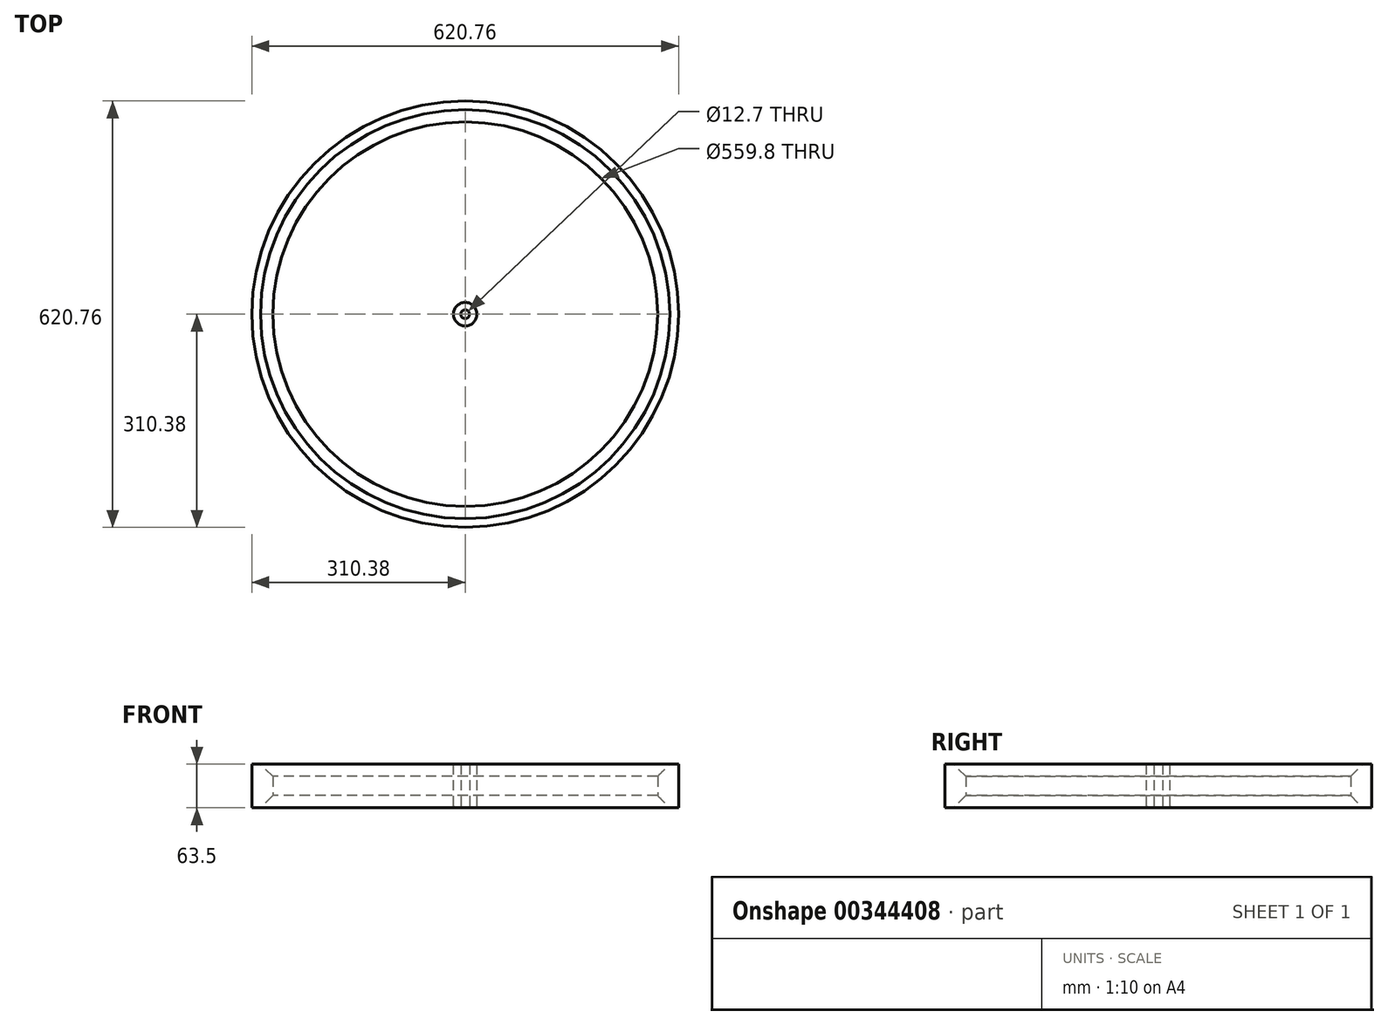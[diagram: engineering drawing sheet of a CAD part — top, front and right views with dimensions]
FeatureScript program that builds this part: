
annotation { "Feature Type Name" : "Feature", "Feature Type Description" : "" }
export const myFeature = defineFeature(function(context is Context, id is Id, definition is map)
    precondition{}
    {
        {
            var Q0;
            Q0=qCreatedBy(makeId("Top.planeOp"),FACE);
            var sketch = newSketch(context, id + "F0", { "sketchPlane" : qUnion([Q0])});
            skCircle(sketch, "E0", {"center": v(0, 0) * mm, "radius": 310.38 * mm});
            skSolve(sketch);
        }
        {
            var Q0;
            Q0=makeQuery(id+"F0.imprint","IMPRINT",FACE,{"disambiguationData":[TD([[makeQuery(id+"F0.imprint","IMPRINT",EDGE,{"derivedFrom":sQuery(id+"F0.wireOp",EDGE,"E0")}),1.0]])]});
            extrude(context, id + "F1", {"entities" : qUnion([Q0]), "endBound" : BoundingType.SYMMETRIC, "depth" : 63.5 * mm});
        }
        {
            var Q0;
            Q0=makeQuery(id+"F1.opExtrude","CAP_FACE",FACE,{"disambiguationData":[OSD([sQuery(id+"F0.wireOp",EDGE,"E0")])],"isStart":false});
            var sketch = newSketch(context, id + "F2", { "sketchPlane" : qUnion([Q0])});
            skCircle(sketch, "E1", {"center": v(0, 0) * mm, "radius": 267.57 * mm});
            skCircle(sketch, "E2", {"center": v(0, 0) * mm, "radius": 17.1 * mm});
            skSolve(sketch);
        }
        {
            var Q0;
            Q0=makeQuery(id+"F1.opExtrude","CAP_FACE",FACE,{"disambiguationData":[OSD([sQuery(id+"F0.wireOp",EDGE,"E0")])],"isStart":false});
            var Q1;
            Q1=makeQuery(id+"F1.opExtrude","CAP_FACE",FACE,{"disambiguationData":[OSD([sQuery(id+"F0.wireOp",EDGE,"E0")])],"isStart":true});
            var Q2;
            Q2=makeQuery(id+"F1.opExtrude","SWEPT_BODY",BODY,{"disambiguationData":[OSD([sQuery(id+"F0.wireOp",EDGE,"E0")])]});
            shell(context, id + "F3", {"entities" : qUnion([Q0, Q1]), "parts" : qUnion([Q2]), "thickness" : 30.48 * mm});
        }
        {
            var Q0;
            Q0=makeQuery(id+"F2.imprint","IMPRINT",FACE,{"disambiguationData":[TD([[makeQuery(id+"F2.imprint","IMPRINT",EDGE,{"derivedFrom":sQuery(id+"F2.wireOp",EDGE,"E2")}),1.0]])]});
            extrude(context, id + "F4", {"entities" : qUnion([Q0]), "oppositeDirection" : true, "depth" : 63.5 * mm});
        }
        {
            var Q0;
            Q0=makeQuery(id+"F4.opExtrude","SWEPT_FACE",FACE,{"disambiguationData":[OSD([sQuery(id+"F2.wireOp",EDGE,"E2")])]});
            fillet(context, id + "F5", {"entities" : qUnion([Q0]), "radius" : 2.54 * mm, "tangentPropagation" : true, "allowEdgeOverflow" : false});
        }
        {
            var Q0;
            Q0=qCreatedBy(makeId("Top.planeOp"),FACE);
            var sketch = newSketch(context, id + "F6", { "sketchPlane" : qUnion([Q0])});
            skLineSegment(sketch, "E3", {"start": v(203.69, 189.84) * mm, "end": v(0, 0) * mm});
            skLineSegment(sketch, "E4", {"start": v(0, 0) * mm, "end": v(0, 279.46) * mm});
            skLineSegment(sketch, "E5", {"start": v(0, 279.46) * mm, "end": v(0, -279.46) * mm});
            skLineSegment(sketch, "E6", {"start": v(0, 0) * mm, "end": v(279.46, 0) * mm});
            skLineSegment(sketch, "E7", {"start": v(279.46, 0) * mm, "end": v(-279.46, 0) * mm});
            skLineSegment(sketch, "E8.MirrorCS", {"start": v(203.69, -189.84) * mm, "end": v(0, 0) * mm});
            skLineSegment(sketch, "E9.MirrorCS", {"start": v(-203.69, 189.84) * mm, "end": v(0, 0) * mm});
            skLineSegment(sketch, "E10.MirrorCS", {"start": v(-203.69, -189.84) * mm, "end": v(0, 0) * mm});
            skLineSegment(sketch, "E11.MirrorCS", {"start": v(-279.46, 0) * mm, "end": v(279.46, 0) * mm});
            skLineSegment(sketch, "E12.MirrorCS", {"start": v(0, -279.46) * mm, "end": v(0, 279.46) * mm});
            skLineSegment(sketch, "E13", {"start": v(263.16, 96.14) * mm, "end": v(0, 0) * mm});
            skLineSegment(sketch, "E14.MirrorCS", {"start": v(263.16, -96.14) * mm, "end": v(0, 0) * mm});
            skLineSegment(sketch, "E15.MirrorCS", {"start": v(-263.16, 96.14) * mm, "end": v(0, 0) * mm});
            skLineSegment(sketch, "E16.MirrorCS", {"start": v(-263.16, -96.14) * mm, "end": v(0, 0) * mm});
            skLineSegment(sketch, "E17", {"start": v(123.37, 250.75) * mm, "end": v(0, 0) * mm});
            skLineSegment(sketch, "E18.MirrorCS", {"start": v(123.37, -250.75) * mm, "end": v(0, 0) * mm});
            skLineSegment(sketch, "E19.MirrorCS", {"start": v(-123.37, 250.75) * mm, "end": v(0, 0) * mm});
            skLineSegment(sketch, "E20.MirrorCS", {"start": v(-123.37, -250.75) * mm, "end": v(0, 0) * mm});
            skArc(sketch, "E21", {"start": v(123.37, 250.75) * mm, "mid": v(63.34, 272.19) * mm, "end": v(0, 279.46) * mm});
            skArc(sketch, "E22", {"start": v(-123.37, 250.75) * mm, "mid": v(-63.34, 272.19) * mm, "end": v(0, 279.46) * mm});
            skArc(sketch, "E23", {"start": v(-203.69, 189.84) * mm, "mid": v(-166.04, 223.51) * mm, "end": v(-122.92, 249.83) * mm});
            skArc(sketch, "E24", {"start": v(-203.69, 189.84) * mm, "mid": v(-237.34, 145.6) * mm, "end": v(-261.53, 95.54) * mm});
            skArc(sketch, "E25", {"start": v(-279.46, 0) * mm, "mid": v(-275.18, 48.7) * mm, "end": v(-262.49, 95.9) * mm});
            skArc(sketch, "E26", {"start": v(203.69, 189.84) * mm, "mid": v(166.04, 223.51) * mm, "end": v(122.92, 249.83) * mm});
            skArc(sketch, "E27.MirrorCS", {"start": v(203.69, 189.84) * mm, "mid": v(237.34, 145.6) * mm, "end": v(261.53, 95.54) * mm});
            skArc(sketch, "E28.MirrorCS", {"start": v(279.46, 0) * mm, "mid": v(275.18, 48.7) * mm, "end": v(262.49, 95.9) * mm});
            skArc(sketch, "E29.MirrorCS", {"start": v(-279.46, 0) * mm, "mid": v(-275.18, -48.7) * mm, "end": v(-262.49, -95.9) * mm});
            skArc(sketch, "E30.MirrorCS", {"start": v(-203.69, -189.84) * mm, "mid": v(-237.34, -145.6) * mm, "end": v(-261.53, -95.54) * mm});
            skArc(sketch, "E31.MirrorCS", {"start": v(-203.69, -189.84) * mm, "mid": v(-166.04, -223.51) * mm, "end": v(-122.92, -249.83) * mm});
            skArc(sketch, "E32.MirrorCS", {"start": v(-123.37, -250.75) * mm, "mid": v(-63.34, -272.19) * mm, "end": v(0, -279.46) * mm});
            skArc(sketch, "E33.MirrorCS", {"start": v(123.37, -250.75) * mm, "mid": v(63.34, -272.19) * mm, "end": v(0, -279.46) * mm});
            skArc(sketch, "E34.MirrorCS", {"start": v(203.69, -189.84) * mm, "mid": v(166.04, -223.51) * mm, "end": v(122.92, -249.83) * mm});
            skArc(sketch, "E35.MirrorCS", {"start": v(203.69, -189.84) * mm, "mid": v(237.34, -145.6) * mm, "end": v(261.53, -95.54) * mm});
            skArc(sketch, "E36.MirrorCS", {"start": v(279.46, 0) * mm, "mid": v(275.18, -48.7) * mm, "end": v(262.49, -95.9) * mm});
            skSolve(sketch);
        }
        {
            var Q0;
            {var subQ0=sQuery(id+"F6.wireOp",EDGE,"E3");Q0=makeQuery(id+"F6.imprint","IMPRINT",FACE,{"disambiguationData":[TD([[makeQuery(id+"F6.imprint","IMPRINT",EDGE,{"derivedFrom":subQ0}),1.0]])]});}
            var Q1;
            {var subQ0=sQuery(id+"F6.wireOp",EDGE,"E3");Q1=makeQuery(id+"F6.imprint","IMPRINT",FACE,{"disambiguationData":[TD([[makeQuery(id+"F6.imprint","IMPRINT",EDGE,{"derivedFrom":subQ0}),-1.0]])]});}
            var Q2;
            {var subQ0=sQuery(id+"F6.wireOp",EDGE,"E21");Q2=makeQuery(id+"F6.imprint","IMPRINT",FACE,{"disambiguationData":[TD([[makeQuery(id+"F6.imprint","IMPRINT",EDGE,{"derivedFrom":subQ0}),1.0]])]});}
            var Q3;
            {var subQ4=sQuery(id+"F6.wireOp",EDGE,"E22");Q3=makeQuery(id+"F6.imprint","IMPRINT",FACE,{"disambiguationData":[TD([[makeQuery(id+"F6.imprint","IMPRINT",EDGE,{"derivedFrom":subQ4}),-1.0]])]});}
            var Q4;
            {var subQ0=sQuery(id+"F6.wireOp",EDGE,"E9.MirrorCS");Q4=makeQuery(id+"F6.imprint","IMPRINT",FACE,{"disambiguationData":[TD([[makeQuery(id+"F6.imprint","IMPRINT",EDGE,{"derivedFrom":subQ0}),1.0]])]});}
            var Q5;
            {var subQ0=sQuery(id+"F6.wireOp",EDGE,"E9.MirrorCS");Q5=makeQuery(id+"F6.imprint","IMPRINT",FACE,{"disambiguationData":[TD([[makeQuery(id+"F6.imprint","IMPRINT",EDGE,{"derivedFrom":subQ0}),-1.0]])]});}
            var Q6;
            {var subQ0=sQuery(id+"F6.wireOp",EDGE,"E25");Q6=makeQuery(id+"F6.imprint","IMPRINT",FACE,{"disambiguationData":[TD([[makeQuery(id+"F6.imprint","IMPRINT",EDGE,{"derivedFrom":subQ0}),-1.0]])]});}
            var Q7;
            {var subQ0=sQuery(id+"F6.wireOp",EDGE,"E29.MirrorCS");Q7=makeQuery(id+"F6.imprint","IMPRINT",FACE,{"disambiguationData":[TD([[makeQuery(id+"F6.imprint","IMPRINT",EDGE,{"derivedFrom":subQ0}),1.0]])]});}
            var Q8;
            {var subQ0=sQuery(id+"F6.wireOp",EDGE,"E10.MirrorCS");Q8=makeQuery(id+"F6.imprint","IMPRINT",FACE,{"disambiguationData":[TD([[makeQuery(id+"F6.imprint","IMPRINT",EDGE,{"derivedFrom":subQ0}),1.0]])]});}
            var Q9;
            {var subQ0=sQuery(id+"F6.wireOp",EDGE,"E10.MirrorCS");Q9=makeQuery(id+"F6.imprint","IMPRINT",FACE,{"disambiguationData":[TD([[makeQuery(id+"F6.imprint","IMPRINT",EDGE,{"derivedFrom":subQ0}),-1.0]])]});}
            var Q10;
            {var subQ4=sQuery(id+"F6.wireOp",EDGE,"E32.MirrorCS");Q10=makeQuery(id+"F6.imprint","IMPRINT",FACE,{"disambiguationData":[TD([[makeQuery(id+"F6.imprint","IMPRINT",EDGE,{"derivedFrom":subQ4}),1.0]])]});}
            var Q11;
            {var subQ4=sQuery(id+"F6.wireOp",EDGE,"E33.MirrorCS");Q11=makeQuery(id+"F6.imprint","IMPRINT",FACE,{"disambiguationData":[TD([[makeQuery(id+"F6.imprint","IMPRINT",EDGE,{"derivedFrom":subQ4}),-1.0]])]});}
            var Q12;
            {var subQ0=sQuery(id+"F6.wireOp",EDGE,"E8.MirrorCS");Q12=makeQuery(id+"F6.imprint","IMPRINT",FACE,{"disambiguationData":[TD([[makeQuery(id+"F6.imprint","IMPRINT",EDGE,{"derivedFrom":subQ0}),1.0]])]});}
            var Q13;
            {var subQ0=sQuery(id+"F6.wireOp",EDGE,"E8.MirrorCS");Q13=makeQuery(id+"F6.imprint","IMPRINT",FACE,{"disambiguationData":[TD([[makeQuery(id+"F6.imprint","IMPRINT",EDGE,{"derivedFrom":subQ0}),-1.0]])]});}
            var Q14;
            {var subQ3=sQuery(id+"F6.wireOp",EDGE,"E36.MirrorCS");Q14=makeQuery(id+"F6.imprint","IMPRINT",FACE,{"disambiguationData":[TD([[makeQuery(id+"F6.imprint","IMPRINT",EDGE,{"derivedFrom":subQ3}),-1.0]])]});}
            var Q15;
            {var subQ3=sQuery(id+"F6.wireOp",EDGE,"E28.MirrorCS");Q15=makeQuery(id+"F6.imprint","IMPRINT",FACE,{"disambiguationData":[TD([[makeQuery(id+"F6.imprint","IMPRINT",EDGE,{"derivedFrom":subQ3}),1.0]])]});}
            var Q16;
            Q16=sQuery(id+"F6.wireOp",EDGE,"E17");
            extrude(context, id + "F7", {"entities" : qUnion([Q0, Q1, Q2, Q3, Q4, Q5, Q6, Q7, Q8, Q9, Q10, Q11, Q12, Q13, Q14, Q15]), "bodyType" : ToolBodyType.SURFACE, "surfaceEntities" : qUnion([Q16]), "depth" : 2.54 * mm});
        }
        {
            var Q0;
            Q0=makeQuery(id+"F7.opExtrude","SWEPT_BODY",BODY,{"disambiguationData":[OSD([sQuery(id+"F6.wireOp",EDGE,"E17")])]});
            var Q1;
            {var subQ0=sQuery(id+"F2.wireOp",EDGE,"E2");Q1=makeQuery(id+"F5.opFillet","BLEND_EDGE",EDGE,{"blendedFrom":[makeQuery(id+"F4.opExtrude","CAP_EDGE",EDGE,{"disambiguationData":[OSD([subQ0])],"isStart":false}),makeQuery(id+"F4.opExtrude","CAP_FACE",FACE,{"disambiguationData":[OSD([subQ0])],"isStart":false})],"blendedInto":[makeQuery(id+"F4.opExtrude","CAP_FACE",FACE,{"disambiguationData":[OSD([subQ0])],"isStart":false})]});}
            circularPattern(context, id + "F8", {"entities" : qUnion([Q0]), "axis" : qUnion([Q1]), "angle" : 360 * degree, "instanceCount" : 25, "equalSpace" : true});
        }
        {
            var Q0;
            {var subQ0=sQuery(id+"F0.wireOp",EDGE,"E0");Q0=makeQuery(id+"F3.opShell","OFFSET_EDGE",EDGE,{"disambiguationData":[OSD([subQ0]),TDD([makeQuery(id+"F1.opExtrude","CAP_EDGE",EDGE,{"disambiguationData":[OSD([subQ0])],"isStart":true})])]});}
            var Q1;
            {var subQ0=sQuery(id+"F0.wireOp",EDGE,"E0");Q1=makeQuery(id+"F3.opShell","OFFSET_EDGE",EDGE,{"disambiguationData":[OSD([subQ0]),TDD([makeQuery(id+"F1.opExtrude","CAP_EDGE",EDGE,{"disambiguationData":[OSD([subQ0])],"isStart":false})])]});}
            chamfer(context, id + "F9", {"entities" : qUnion([Q0, Q1]), "width" : 17.78 * mm, "tangentPropagation" : true});
        }
        {
            var Q0;
            Q0=makeQuery(id+"F4.opExtrude","CAP_FACE",FACE,{"disambiguationData":[OSD([sQuery(id+"F2.wireOp",EDGE,"E2")])],"isStart":false});
            var sketch = newSketch(context, id + "F10", { "sketchPlane" : qUnion([Q0])});
            skCircle(sketch, "E37", {"center": v(0, 0) * mm, "radius": 45.59 * mm});
            skSolve(sketch);
        }
        {
            var Q0;
            Q0=sQuery(id+"F10.wireOp",VERTEX,"E37.center");
            var Q1;
            Q1=makeQuery(id+"F4.opExtrude","SWEPT_BODY",BODY,{"disambiguationData":[OSD([sQuery(id+"F2.wireOp",EDGE,"E2")])]});
            hole(context, id + "F11", {"style" : HoleStyle.SIMPLE, "endStyle" : HoleEndStyle.THROUGH, "holeDiameter" : 12.7 * mm, "isTappedThrough" : true, "tappedDepth" : 12.7 * mm, "tapClearance" : 3, "locations" : qUnion([Q0]), "scope" : qUnion([Q1])});
        }
    });
